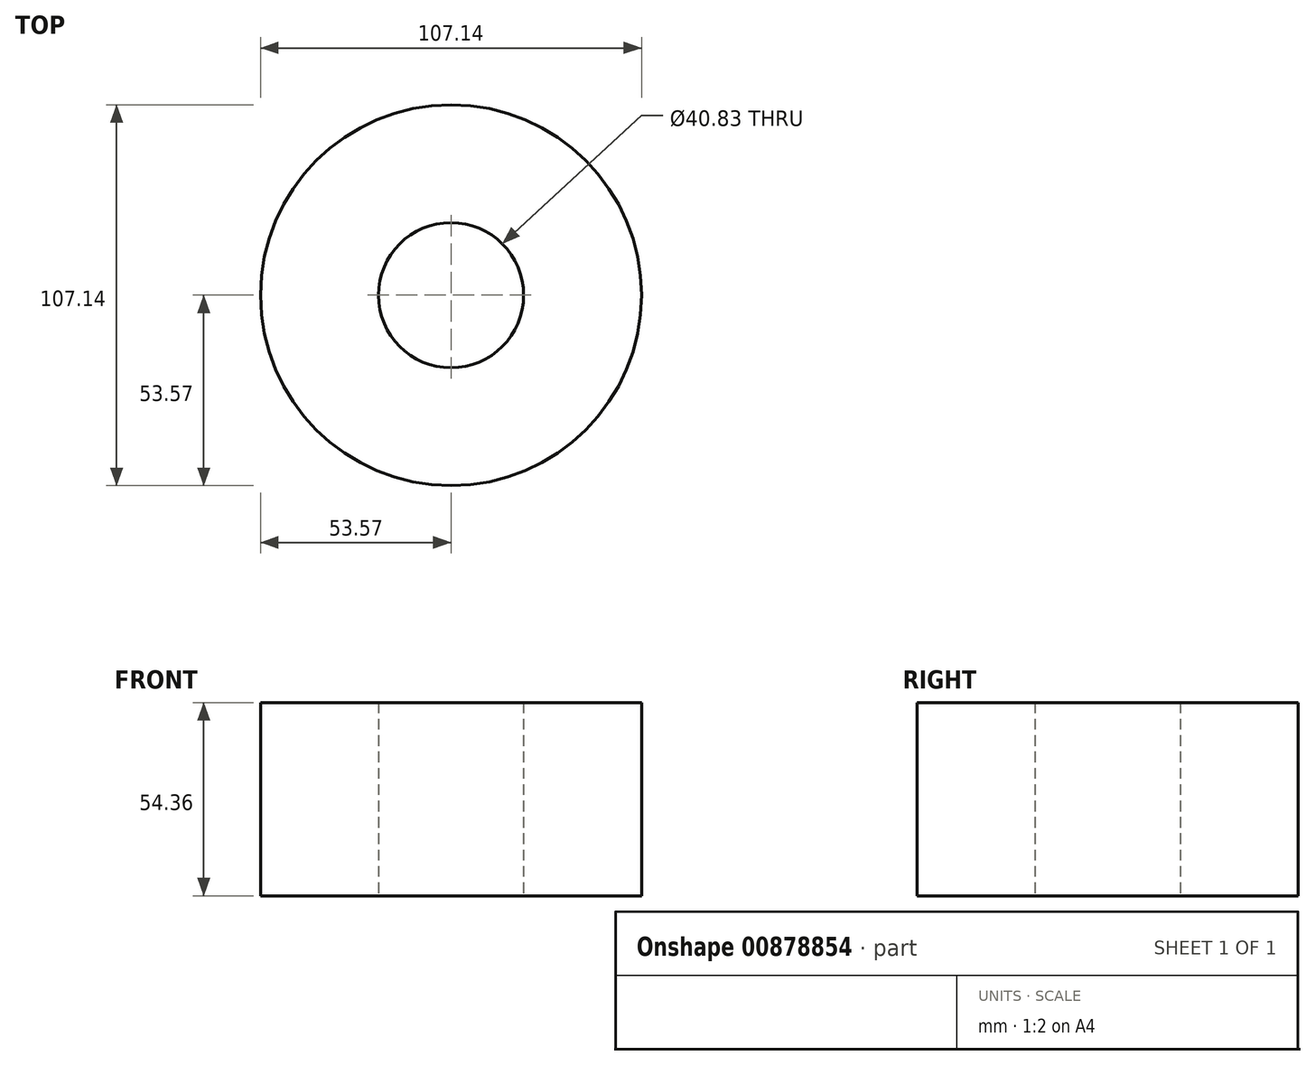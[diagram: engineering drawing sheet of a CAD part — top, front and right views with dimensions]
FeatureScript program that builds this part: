
annotation { "Feature Type Name" : "Feature", "Feature Type Description" : "" }
export const myFeature = defineFeature(function(context is Context, id is Id, definition is map)
    precondition{}
    {
        {
            var Q0;
            Q0=qCreatedBy(makeId("Top.planeOp"),FACE);
            var sketch = newSketch(context, id + "F0", { "sketchPlane" : qUnion([Q0])});
            skCircle(sketch, "E0", {"center": v(0, 0) * mm, "radius": 53.57 * mm});
            skCircle(sketch, "E1", {"center": v(0, 0) * mm, "radius": 20.41 * mm});
            skSolve(sketch);
        }
        {
            var Q0;
            Q0 = qSketchRegion(id + "F0", true);
            extrude(context, id + "F1", {"entities" : qUnion([Q0]), "depth" : 54.36 * mm, "offsetDistance" : 25.4 * mm});
        }
    });
